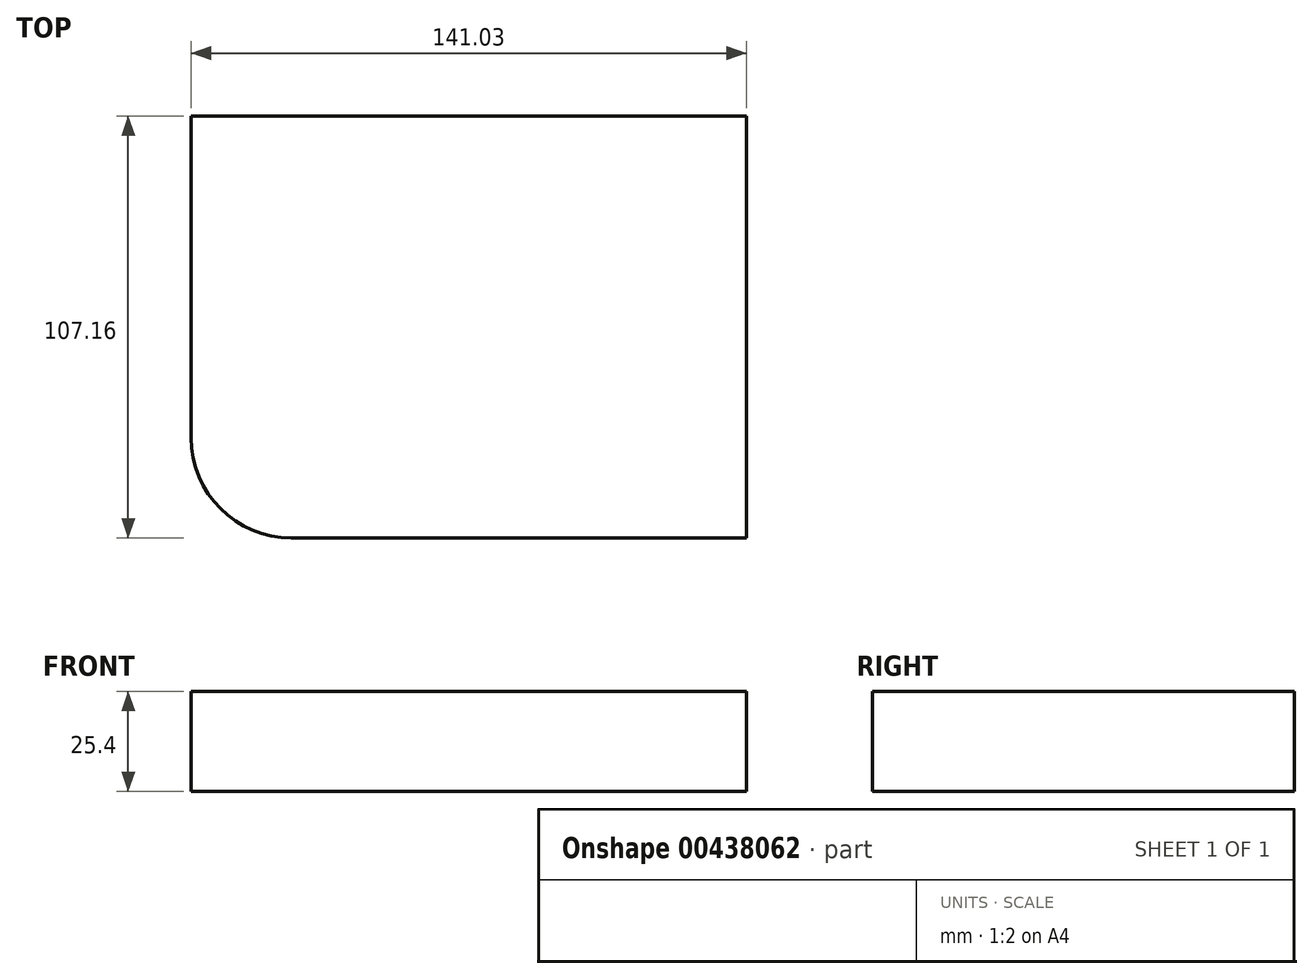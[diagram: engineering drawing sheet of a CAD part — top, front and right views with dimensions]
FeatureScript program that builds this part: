
annotation { "Feature Type Name" : "Feature", "Feature Type Description" : "" }
export const myFeature = defineFeature(function(context is Context, id is Id, definition is map)
    precondition{}
    {
        {
            var Q0;
            Q0=qCreatedBy(makeId("Top.planeOp"),FACE);
            var sketch = newSketch(context, id + "F0", { "sketchPlane" : qUnion([Q0])});
            skLineSegment(sketch, "E0.bottom", {"start": v(0, 0) * mm, "end": v(0, 0) * mm});
            skLineSegment(sketch, "E0.top", {"start": v(0, -107.16) * mm, "end": v(0, -107.16) * mm});
            skLineSegment(sketch, "E0.left", {"start": v(0, 0) * mm, "end": v(0, -107.16) * mm});
            skLineSegment(sketch, "E0.right", {"start": v(0, 0) * mm, "end": v(0, -107.16) * mm});
            skLineSegment(sketch, "E1.bottom", {"start": v(0, -107.16) * mm, "end": v(-141.03, -107.16) * mm});
            skLineSegment(sketch, "E1.top", {"start": v(0, 0) * mm, "end": v(-141.03, 0) * mm});
            skLineSegment(sketch, "E1.left", {"start": v(0, -107.16) * mm, "end": v(0, 0) * mm});
            skLineSegment(sketch, "E1.right", {"start": v(-141.03, -107.16) * mm, "end": v(-141.03, 0) * mm});
            skSolve(sketch);
        }
        {
            var Q0;
            Q0=makeQuery(id+"F0.imprint","IMPRINT",FACE,{"disambiguationData":[TD([[makeQuery(id+"F0.imprint","IMPRINT",EDGE,{"derivedFrom":sQuery(id+"F0.wireOp",EDGE,"E1.bottom")}),-1.0]])]});
            extrude(context, id + "F1", {"entities" : qUnion([Q0]), "depth" : 25.4 * mm});
        }
        {
            var Q0;
            Q0=makeQuery(id+"F1.opExtrude","SWEPT_EDGE",EDGE,{"disambiguationData":[OSD([sQuery(id+"F0.wireOp",EDGE,"E1.bottom"),sQuery(id+"F0.wireOp",EDGE,"E1.right")])]});
            fillet(context, id + "F2", {"entities" : qUnion([Q0]), "radius" : 25.4 * mm, "tangentPropagation" : true, "allowEdgeOverflow" : false});
        }
    });
